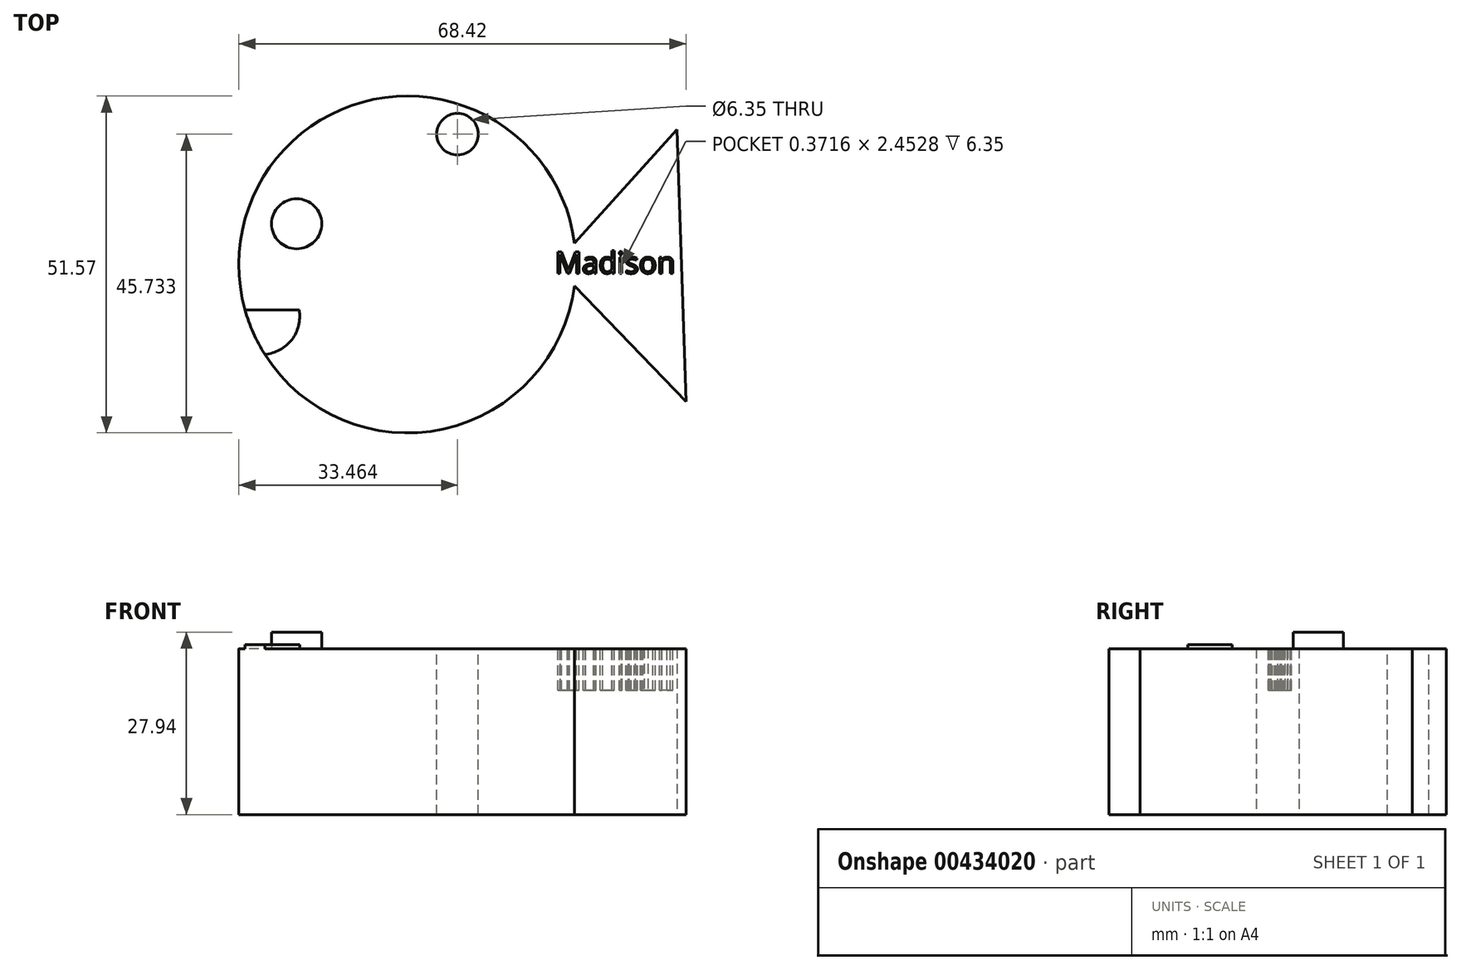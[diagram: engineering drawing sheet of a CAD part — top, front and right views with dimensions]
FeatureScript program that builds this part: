
annotation { "Feature Type Name" : "Feature", "Feature Type Description" : "" }
export const myFeature = defineFeature(function(context is Context, id is Id, definition is map)
    precondition{}
    {
        {
            var Q0;
            Q0=qCreatedBy(makeId("Top.planeOp"),FACE);
            var sketch = newSketch(context, id + "F0", { "sketchPlane" : qUnion([Q0])});
            skArc(sketch, "E0", {"start": v(55.36, 45.54) * mm, "mid": v(4, 42.23) * mm, "end": v(55.36, 38.98) * mm});
            skLineSegment(sketch, "E1", {"start": v(55.36, 45.54) * mm, "end": v(71.06, 62.88) * mm});
            skLineSegment(sketch, "E2", {"start": v(71.06, 62.88) * mm, "end": v(72.42, 21.22) * mm});
            skLineSegment(sketch, "E3", {"start": v(72.42, 21.22) * mm, "end": v(55.36, 38.98) * mm});
            skSolve(sketch);
        }
        {
            var Q0;
            Q0=makeQuery(id+"F0.imprint","IMPRINT",FACE,{"disambiguationData":[TD([[makeQuery(id+"F0.imprint","IMPRINT",EDGE,{"derivedFrom":sQuery(id+"F0.wireOp",EDGE,"E0")}),1.0]])]});
            extrude(context, id + "F1", {"entities" : qUnion([Q0]), "depth" : 25.4 * mm});
        }
        {
            var Q0;
            Q0=makeQuery(id+"F1.opExtrude","CAP_FACE",FACE,{"disambiguationData":[OSD([sQuery(id+"F0.wireOp",EDGE,"E0"),sQuery(id+"F0.wireOp",EDGE,"E1"),sQuery(id+"F0.wireOp",EDGE,"E2"),sQuery(id+"F0.wireOp",EDGE,"E3")])],"isStart":false});
            var sketch = newSketch(context, id + "F2", { "sketchPlane" : qUnion([Q0])});
            skCircle(sketch, "E4", {"center": v(12.85, 48.47) * mm, "radius": 3.83 * mm});
            skSolve(sketch);
        }
        {
            var Q0;
            Q0=makeQuery(id+"F2.imprint","IMPRINT",FACE,{"disambiguationData":[TD([[makeQuery(id+"F2.imprint","IMPRINT",EDGE,{"derivedFrom":sQuery(id+"F2.wireOp",EDGE,"E4")}),1.0]])]});
            extrude(context, id + "F3", {"entities" : qUnion([Q0]), "operationType" : NewBodyOperationType.ADD, "depth" : 2.54 * mm});
        }
        {
            var Q0;
            Q0=makeQuery(id+"F1.opExtrude","CAP_FACE",FACE,{"disambiguationData":[OSD([sQuery(id+"F0.wireOp",EDGE,"E0"),sQuery(id+"F0.wireOp",EDGE,"E1"),sQuery(id+"F0.wireOp",EDGE,"E2"),sQuery(id+"F0.wireOp",EDGE,"E3")])],"isStart":false});
            var sketch = newSketch(context, id + "F4", { "sketchPlane" : qUnion([Q0])});
            skLineSegment(sketch, "E5", {"start": v(4.95, 35.3) * mm, "end": v(13.24, 35.3) * mm});
            skArc(sketch, "E6", {"start": v(7.98, 28.48) * mm, "mid": v(12.1, 30.74) * mm, "end": v(13.24, 35.3) * mm});
            skSolve(sketch);
        }
        {
            var Q0;
            {var subQ0=sQuery(id+"F4.wireOp",EDGE,"E5");Q0=makeQuery(id+"F4.imprint","IMPRINT",FACE,{"disambiguationData":[TD([[makeQuery(id+"F4.imprint","IMPRINT",EDGE,{"derivedFrom":subQ0}),-1.0]])]});}
            extrude(context, id + "F5", {"entities" : qUnion([Q0]), "operationType" : NewBodyOperationType.ADD, "depth" : 0.64 * mm});
        }
        {
            var Q0;
            Q0=makeQuery(id+"F1.opExtrude","CAP_FACE",FACE,{"disambiguationData":[OSD([sQuery(id+"F0.wireOp",EDGE,"E0"),sQuery(id+"F0.wireOp",EDGE,"E1"),sQuery(id+"F0.wireOp",EDGE,"E2"),sQuery(id+"F0.wireOp",EDGE,"E3")])],"isStart":false});
            var sketch = newSketch(context, id + "F6", { "sketchPlane" : qUnion([Q0])});
            skText(sketch, "E7", { "text": "Madison", "fontName": "OpenSans-Regular.ttf"});
            const initialGuessF6  = {"E7": [0.05237, 0.04088, 1, 0, 0.0033]};
            skSetInitialGuess(sketch, initialGuessF6);
            skSolve(sketch);
        }
        {
            var Q0;
            Q0 = qSketchRegion(id + "F6", true);
            extrude(context, id + "F7", {"entities" : qUnion([Q0]), "operationType" : NewBodyOperationType.REMOVE, "oppositeDirection" : true, "depth" : 6.35 * mm});
        }
        {
            var Q0;
            {var subQ0=sQuery(id+"F0.wireOp",EDGE,"E3");var subQ1=sQuery(id+"F0.wireOp",EDGE,"E2");var subQ2=sQuery(id+"F0.wireOp",EDGE,"E1");var subQ3=sQuery(id+"F0.wireOp",EDGE,"E0");Q0=makeQuery(id+"F7.boolean.opBoolean","SPLIT",FACE,{"disambiguationData":[TD([makeQuery(id+"F1.opExtrude","SWEPT_FACE",FACE,{"disambiguationData":[OSD([subQ3])]})])],"derivedFrom":makeQuery(id+"F1.opExtrude","CAP_FACE",FACE,{"disambiguationData":[OSD([subQ3,subQ2,subQ1,subQ0])],"isStart":false})});}
            var sketch = newSketch(context, id + "F8", { "sketchPlane" : qUnion([Q0])});
            skCircle(sketch, "E8", {"center": v(37.46, 62.2) * mm, "radius": 3.18 * mm});
            skSolve(sketch);
        }
        {
            var Q0;
            Q0 = qSketchRegion(id + "F8", true);
            extrude(context, id + "F9", {"entities" : qUnion([Q0]), "operationType" : NewBodyOperationType.REMOVE, "oppositeDirection" : true, "depth" : 25.4 * mm});
        }
    });
